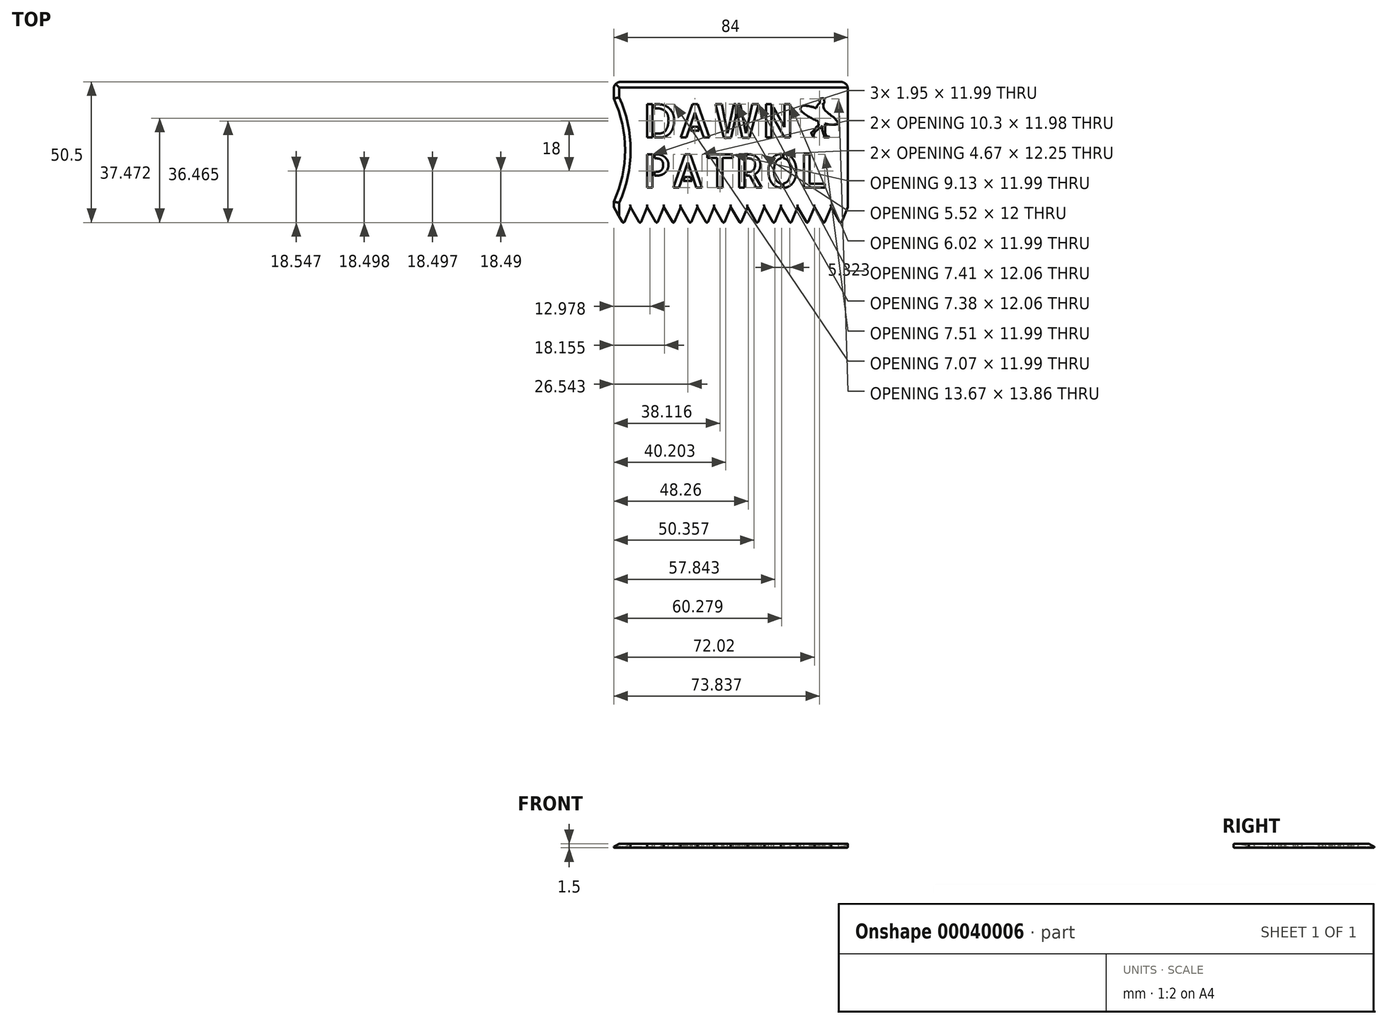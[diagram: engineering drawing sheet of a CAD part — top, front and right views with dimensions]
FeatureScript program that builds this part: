
annotation { "Feature Type Name" : "Feature", "Feature Type Description" : "" }
export const myFeature = defineFeature(function(context is Context, id is Id, definition is map)
    precondition{}
    {
        {
            assignVariable(context, id + "F0", {"name" : "t", "anyValue" : 1.5});
        }
        {
            var Q0;
            Q0=qCreatedBy(makeId("Top.planeOp"),FACE);
            var sketch = newSketch(context, id + "F1", { "sketchPlane" : qUnion([Q0])});
            skLineSegment(sketch, "E0.bottom", {"start": v(84, 51) * mm, "end": v(0, 51) * mm});
            skLineSegment(sketch, "E0.top", {"start": v(81.5, 0) * mm, "end": v(3.5, 0) * mm, "construction": true});
            skLineSegment(sketch, "E0.left", {"start": v(84, 51) * mm, "end": v(84, 6) * mm});
            skLineSegment(sketch, "E0.right", {"start": v(0, 51) * mm, "end": v(0, 6) * mm, "construction": true});
            skLineSegment(sketch, "E1", {"start": v(84, 6) * mm, "end": v(0, 6) * mm, "construction": true});
            skLineSegment(sketch, "E2", {"start": v(84, 6) * mm, "end": v(81.5, 0) * mm});
            skLineSegment(sketch, "E3", {"start": v(81.5, 0) * mm, "end": v(78, 6) * mm});
            skLineSegment(sketch, "E4.1.0.0", {"start": v(78, 6) * mm, "end": v(75.5, 0) * mm});
            skLineSegment(sketch, "E4.1.0.1", {"start": v(75.5, 0) * mm, "end": v(72, 6) * mm});
            skLineSegment(sketch, "E4.2.0.0", {"start": v(72, 6) * mm, "end": v(69.5, 0) * mm});
            skLineSegment(sketch, "E4.2.0.1", {"start": v(69.5, 0) * mm, "end": v(66, 6) * mm});
            skLineSegment(sketch, "E4.3.0.0", {"start": v(66, 6) * mm, "end": v(63.5, 0) * mm});
            skLineSegment(sketch, "E4.3.0.1", {"start": v(63.5, 0) * mm, "end": v(60, 6) * mm});
            skLineSegment(sketch, "E4.4.0.0", {"start": v(60, 6) * mm, "end": v(57.5, 0) * mm});
            skLineSegment(sketch, "E4.4.0.1", {"start": v(57.5, 0) * mm, "end": v(54, 6) * mm});
            skLineSegment(sketch, "E4.5.0.0", {"start": v(54, 6) * mm, "end": v(51.5, 0) * mm});
            skLineSegment(sketch, "E4.5.0.1", {"start": v(51.5, 0) * mm, "end": v(48, 6) * mm});
            skLineSegment(sketch, "E4.6.0.0", {"start": v(48, 6) * mm, "end": v(45.5, 0) * mm});
            skLineSegment(sketch, "E4.6.0.1", {"start": v(45.5, 0) * mm, "end": v(42, 6) * mm});
            skLineSegment(sketch, "E4.7.0.0", {"start": v(42, 6) * mm, "end": v(39.5, 0) * mm});
            skLineSegment(sketch, "E4.7.0.1", {"start": v(39.5, 0) * mm, "end": v(36, 6) * mm});
            skLineSegment(sketch, "E4.8.0.0", {"start": v(36, 6) * mm, "end": v(33.5, 0) * mm});
            skLineSegment(sketch, "E4.8.0.1", {"start": v(33.5, 0) * mm, "end": v(30, 6) * mm});
            skLineSegment(sketch, "E4.9.0.0", {"start": v(30, 6) * mm, "end": v(27.5, 0) * mm});
            skLineSegment(sketch, "E4.9.0.1", {"start": v(27.5, 0) * mm, "end": v(24, 6) * mm});
            skLineSegment(sketch, "E4.10.0.0", {"start": v(24, 6) * mm, "end": v(21.5, 0) * mm});
            skLineSegment(sketch, "E4.10.0.1", {"start": v(21.5, 0) * mm, "end": v(18, 6) * mm});
            skLineSegment(sketch, "E4.11.0.0", {"start": v(18, 6) * mm, "end": v(15.5, 0) * mm});
            skLineSegment(sketch, "E4.11.0.1", {"start": v(15.5, 0) * mm, "end": v(12, 6) * mm});
            skLineSegment(sketch, "E4.12.0.0", {"start": v(12, 6) * mm, "end": v(9.5, 0) * mm});
            skLineSegment(sketch, "E4.12.0.1", {"start": v(9.5, 0) * mm, "end": v(6, 6) * mm});
            skLineSegment(sketch, "E4.13.0.0", {"start": v(6, 6) * mm, "end": v(3.5, 0) * mm});
            skLineSegment(sketch, "E4.13.0.1", {"start": v(3.5, 0) * mm, "end": v(0, 6) * mm});
            skLineSegment(sketch, "E4.direction1", {"start": v(84, 6) * mm, "end": v(78, 6) * mm, "construction": true});
            skLineSegment(sketch, "E5", {"start": v(0, 6) * mm, "end": v(0, 8) * mm});
            skArc(sketch, "E6", {"start": v(0, 8) * mm, "mid": v(4.07, 26.5) * mm, "end": v(0, 45) * mm});
            skLineSegment(sketch, "E7", {"start": v(0, 45) * mm, "end": v(0, 51) * mm});
            skLineSegment(sketch, "E8", {"start": v(0, 6) * mm, "end": v(0, 0) * mm, "construction": true});
            skSolve(sketch);
        }
        {
            var Q0;
            Q0=qSketchRegion(id+"F1",true);
            extrude(context, id + "F2", {"entities" : qUnion([Q0]), "depth" : (getVariable(context, 't')) * mm});
        }
        {
            var Q0;
            Q0=makeQuery(id+"F2.opExtrude","CAP_EDGE",EDGE,{"disambiguationData":[OSD([sQuery(id+"F1.wireOp",EDGE,"E5")])],"isStart":false});
            var Q1;
            Q1=makeQuery(id+"F2.opExtrude","CAP_EDGE",EDGE,{"disambiguationData":[OSD([sQuery(id+"F1.wireOp",EDGE,"E6")])],"isStart":false});
            var Q2;
            Q2=makeQuery(id+"F2.opExtrude","CAP_EDGE",EDGE,{"disambiguationData":[OSD([sQuery(id+"F1.wireOp",EDGE,"E0.bottom")])],"isStart":false});
            var Q3;
            Q3=makeQuery(id+"F2.opExtrude","CAP_EDGE",EDGE,{"disambiguationData":[OSD([sQuery(id+"F1.wireOp",EDGE,"E7")])],"isStart":false});
            chamfer(context, id + "F3", {"entities" : qUnion([Q0, Q1, Q2, Q3]), "chamferType" : ChamferType.TWO_OFFSETS, "width1" : (getVariable(context, 't') * 2.2 / 3) * mm, "oppositeDirection" : false, "width2" : (getVariable(context, 't') * 4 / 3) * mm, "tangentPropagation" : true});
        }
        {
            var Q0;
            Q0=makeQuery(id+"F2.opExtrude","SWEPT_EDGE",EDGE,{"disambiguationData":[OSD([sQuery(id+"F1.wireOp",EDGE,"E0.bottom"),sQuery(id+"F1.wireOp",EDGE,"E7")])]});
            var Q1;
            Q1=makeQuery(id+"F2.opExtrude","SWEPT_EDGE",EDGE,{"disambiguationData":[OSD([sQuery(id+"F1.wireOp",EDGE,"E0.bottom"),sQuery(id+"F1.wireOp",EDGE,"E0.left")])]});
            fillet(context, id + "F4", {"entities" : qUnion([Q0, Q1]), "radius" : 2.5 * mm, "tangentPropagation" : true, "allowEdgeOverflow" : false});
        }
        {
            var Q0;
            Q0=makeQuery(id+"F2.opExtrude","CAP_FACE",FACE,{"disambiguationData":[OSD([sQuery(id+"F1.wireOp",EDGE,"E0.bottom"),sQuery(id+"F1.wireOp",EDGE,"E0.left"),sQuery(id+"F1.wireOp",EDGE,"E2"),sQuery(id+"F1.wireOp",EDGE,"E3"),sQuery(id+"F1.wireOp",EDGE,"E4.1.0.0"),sQuery(id+"F1.wireOp",EDGE,"E4.1.0.1"),sQuery(id+"F1.wireOp",EDGE,"E4.2.0.0"),sQuery(id+"F1.wireOp",EDGE,"E4.2.0.1"),sQuery(id+"F1.wireOp",EDGE,"E4.3.0.0"),sQuery(id+"F1.wireOp",EDGE,"E4.3.0.1"),sQuery(id+"F1.wireOp",EDGE,"E4.4.0.0"),sQuery(id+"F1.wireOp",EDGE,"E4.4.0.1"),sQuery(id+"F1.wireOp",EDGE,"E4.5.0.0"),sQuery(id+"F1.wireOp",EDGE,"E4.5.0.1"),sQuery(id+"F1.wireOp",EDGE,"E4.6.0.0"),sQuery(id+"F1.wireOp",EDGE,"E4.6.0.1"),sQuery(id+"F1.wireOp",EDGE,"E4.7.0.0"),sQuery(id+"F1.wireOp",EDGE,"E4.7.0.1"),sQuery(id+"F1.wireOp",EDGE,"E4.8.0.0"),sQuery(id+"F1.wireOp",EDGE,"E4.8.0.1"),sQuery(id+"F1.wireOp",EDGE,"E4.9.0.0"),sQuery(id+"F1.wireOp",EDGE,"E4.9.0.1"),sQuery(id+"F1.wireOp",EDGE,"E4.10.0.0"),sQuery(id+"F1.wireOp",EDGE,"E4.10.0.1"),sQuery(id+"F1.wireOp",EDGE,"E4.11.0.0"),sQuery(id+"F1.wireOp",EDGE,"E4.11.0.1"),sQuery(id+"F1.wireOp",EDGE,"E4.12.0.0"),sQuery(id+"F1.wireOp",EDGE,"E4.12.0.1"),sQuery(id+"F1.wireOp",EDGE,"E4.13.0.0"),sQuery(id+"F1.wireOp",EDGE,"E4.13.0.1"),sQuery(id+"F1.wireOp",EDGE,"E5"),sQuery(id+"F1.wireOp",EDGE,"E6"),sQuery(id+"F1.wireOp",EDGE,"E7")])],"isStart":false});
            var sketch = newSketch(context, id + "F5", { "sketchPlane" : qUnion([Q0])});
            skLineSegment(sketch, "E9.0", {"start": v(81.9, 6.42) * mm, "end": v(81.9, 46.9) * mm});
            skLineSegment(sketch, "E9.1", {"start": v(81.19, 4.7) * mm, "end": v(81.9, 6.42) * mm});
            skLineSegment(sketch, "E9.2", {"start": v(77.69, 10.7) * mm, "end": v(81.19, 4.7) * mm});
            skLineSegment(sketch, "E9.3", {"start": v(75.19, 4.7) * mm, "end": v(77.69, 10.7) * mm});
            skLineSegment(sketch, "E9.4", {"start": v(71.69, 10.7) * mm, "end": v(75.19, 4.7) * mm});
            skLineSegment(sketch, "E9.5", {"start": v(69.19, 4.7) * mm, "end": v(71.69, 10.7) * mm});
            skLineSegment(sketch, "E9.6", {"start": v(65.69, 10.7) * mm, "end": v(69.19, 4.7) * mm});
            skLineSegment(sketch, "E9.7", {"start": v(81.9, 46.9) * mm, "end": v(3.64, 46.9) * mm});
            skArc(sketch, "E9.8", {"start": v(3.64, 46.9) * mm, "mid": v(8.1, 29.09) * mm, "end": v(5.57, 10.9) * mm});
            skLineSegment(sketch, "E9.9", {"start": v(5.57, 10.9) * mm, "end": v(9.19, 4.7) * mm});
            skLineSegment(sketch, "E9.10", {"start": v(9.19, 4.7) * mm, "end": v(11.69, 10.7) * mm});
            skLineSegment(sketch, "E9.11", {"start": v(11.69, 10.7) * mm, "end": v(15.19, 4.7) * mm});
            skLineSegment(sketch, "E9.12", {"start": v(15.19, 4.7) * mm, "end": v(17.69, 10.7) * mm});
            skLineSegment(sketch, "E9.13", {"start": v(17.69, 10.7) * mm, "end": v(21.19, 4.7) * mm});
            skLineSegment(sketch, "E9.14", {"start": v(21.19, 4.7) * mm, "end": v(23.69, 10.7) * mm});
            skLineSegment(sketch, "E9.15", {"start": v(23.69, 10.7) * mm, "end": v(27.19, 4.7) * mm});
            skLineSegment(sketch, "E9.16", {"start": v(27.19, 4.7) * mm, "end": v(29.69, 10.7) * mm});
            skLineSegment(sketch, "E9.17", {"start": v(29.69, 10.7) * mm, "end": v(33.19, 4.7) * mm});
            skLineSegment(sketch, "E9.18", {"start": v(33.19, 4.7) * mm, "end": v(35.69, 10.7) * mm});
            skLineSegment(sketch, "E9.19", {"start": v(35.69, 10.7) * mm, "end": v(39.19, 4.7) * mm});
            skLineSegment(sketch, "E9.20", {"start": v(39.19, 4.7) * mm, "end": v(41.69, 10.7) * mm});
            skLineSegment(sketch, "E9.21", {"start": v(41.69, 10.7) * mm, "end": v(45.19, 4.7) * mm});
            skLineSegment(sketch, "E9.22", {"start": v(45.19, 4.7) * mm, "end": v(47.69, 10.7) * mm});
            skLineSegment(sketch, "E9.23", {"start": v(47.69, 10.7) * mm, "end": v(51.19, 4.7) * mm});
            skLineSegment(sketch, "E9.24", {"start": v(51.19, 4.7) * mm, "end": v(53.69, 10.7) * mm});
            skLineSegment(sketch, "E9.25", {"start": v(53.69, 10.7) * mm, "end": v(57.19, 4.7) * mm});
            skLineSegment(sketch, "E9.26", {"start": v(57.19, 4.7) * mm, "end": v(59.69, 10.7) * mm});
            skLineSegment(sketch, "E9.27", {"start": v(59.69, 10.7) * mm, "end": v(63.19, 4.7) * mm});
            skLineSegment(sketch, "E9.28", {"start": v(63.19, 4.7) * mm, "end": v(65.69, 10.7) * mm});
            skSolve(sketch);
        }
        {
            var Q0;
            Q0=makeQuery(id+"F2.opExtrude","CAP_FACE",FACE,{"disambiguationData":[OSD([sQuery(id+"F1.wireOp",EDGE,"E0.bottom"),sQuery(id+"F1.wireOp",EDGE,"E0.left"),sQuery(id+"F1.wireOp",EDGE,"E2"),sQuery(id+"F1.wireOp",EDGE,"E3"),sQuery(id+"F1.wireOp",EDGE,"E4.1.0.0"),sQuery(id+"F1.wireOp",EDGE,"E4.1.0.1"),sQuery(id+"F1.wireOp",EDGE,"E4.2.0.0"),sQuery(id+"F1.wireOp",EDGE,"E4.2.0.1"),sQuery(id+"F1.wireOp",EDGE,"E4.3.0.0"),sQuery(id+"F1.wireOp",EDGE,"E4.3.0.1"),sQuery(id+"F1.wireOp",EDGE,"E4.4.0.0"),sQuery(id+"F1.wireOp",EDGE,"E4.4.0.1"),sQuery(id+"F1.wireOp",EDGE,"E4.5.0.0"),sQuery(id+"F1.wireOp",EDGE,"E4.5.0.1"),sQuery(id+"F1.wireOp",EDGE,"E4.6.0.0"),sQuery(id+"F1.wireOp",EDGE,"E4.6.0.1"),sQuery(id+"F1.wireOp",EDGE,"E4.7.0.0"),sQuery(id+"F1.wireOp",EDGE,"E4.7.0.1"),sQuery(id+"F1.wireOp",EDGE,"E4.8.0.0"),sQuery(id+"F1.wireOp",EDGE,"E4.8.0.1"),sQuery(id+"F1.wireOp",EDGE,"E4.9.0.0"),sQuery(id+"F1.wireOp",EDGE,"E4.9.0.1"),sQuery(id+"F1.wireOp",EDGE,"E4.10.0.0"),sQuery(id+"F1.wireOp",EDGE,"E4.10.0.1"),sQuery(id+"F1.wireOp",EDGE,"E4.11.0.0"),sQuery(id+"F1.wireOp",EDGE,"E4.11.0.1"),sQuery(id+"F1.wireOp",EDGE,"E4.12.0.0"),sQuery(id+"F1.wireOp",EDGE,"E4.12.0.1"),sQuery(id+"F1.wireOp",EDGE,"E4.13.0.0"),sQuery(id+"F1.wireOp",EDGE,"E4.13.0.1"),sQuery(id+"F1.wireOp",EDGE,"E5"),sQuery(id+"F1.wireOp",EDGE,"E6"),sQuery(id+"F1.wireOp",EDGE,"E7")])],"isStart":true});
            var Q1;
            Q1=makeQuery(id+"F2.opExtrude","CAP_EDGE",EDGE,{"disambiguationData":[OSD([sQuery(id+"F1.wireOp",EDGE,"E4.13.0.1")])],"isStart":false});
            var Q2;
            Q2=makeQuery(id+"F2.opExtrude","CAP_EDGE",EDGE,{"disambiguationData":[OSD([sQuery(id+"F1.wireOp",EDGE,"E4.13.0.0")])],"isStart":false});
            var Q3;
            Q3=makeQuery(id+"F2.opExtrude","SWEPT_EDGE",EDGE,{"disambiguationData":[OSD([sQuery(id+"F1.wireOp",EDGE,"E4.13.0.0"),sQuery(id+"F1.wireOp",EDGE,"E4.13.0.1")])]});
            var Q4;
            Q4=makeQuery(id+"F2.opExtrude","CAP_EDGE",EDGE,{"disambiguationData":[OSD([sQuery(id+"F1.wireOp",EDGE,"E4.12.0.1")])],"isStart":false});
            var Q5;
            Q5=makeQuery(id+"F2.opExtrude","SWEPT_EDGE",EDGE,{"disambiguationData":[OSD([sQuery(id+"F1.wireOp",EDGE,"E4.12.0.0"),sQuery(id+"F1.wireOp",EDGE,"E4.12.0.1")])]});
            var Q6;
            Q6=makeQuery(id+"F2.opExtrude","CAP_EDGE",EDGE,{"disambiguationData":[OSD([sQuery(id+"F1.wireOp",EDGE,"E4.12.0.0")])],"isStart":false});
            var Q7;
            Q7=makeQuery(id+"F2.opExtrude","CAP_EDGE",EDGE,{"disambiguationData":[OSD([sQuery(id+"F1.wireOp",EDGE,"E4.11.0.1")])],"isStart":false});
            var Q8;
            Q8=makeQuery(id+"F2.opExtrude","SWEPT_EDGE",EDGE,{"disambiguationData":[OSD([sQuery(id+"F1.wireOp",EDGE,"E4.11.0.0"),sQuery(id+"F1.wireOp",EDGE,"E4.11.0.1")])]});
            var Q9;
            Q9=makeQuery(id+"F2.opExtrude","CAP_EDGE",EDGE,{"disambiguationData":[OSD([sQuery(id+"F1.wireOp",EDGE,"E4.11.0.0")])],"isStart":false});
            var Q10;
            Q10=makeQuery(id+"F2.opExtrude","CAP_EDGE",EDGE,{"disambiguationData":[OSD([sQuery(id+"F1.wireOp",EDGE,"E4.10.0.1")])],"isStart":false});
            var Q11;
            Q11=makeQuery(id+"F2.opExtrude","CAP_EDGE",EDGE,{"disambiguationData":[OSD([sQuery(id+"F1.wireOp",EDGE,"E4.10.0.0")])],"isStart":false});
            var Q12;
            Q12=makeQuery(id+"F2.opExtrude","CAP_EDGE",EDGE,{"disambiguationData":[OSD([sQuery(id+"F1.wireOp",EDGE,"E4.9.0.1")])],"isStart":false});
            var Q13;
            Q13=makeQuery(id+"F2.opExtrude","CAP_EDGE",EDGE,{"disambiguationData":[OSD([sQuery(id+"F1.wireOp",EDGE,"E4.9.0.0")])],"isStart":false});
            var Q14;
            Q14=makeQuery(id+"F2.opExtrude","CAP_EDGE",EDGE,{"disambiguationData":[OSD([sQuery(id+"F1.wireOp",EDGE,"E4.8.0.1")])],"isStart":false});
            var Q15;
            Q15=makeQuery(id+"F2.opExtrude","CAP_EDGE",EDGE,{"disambiguationData":[OSD([sQuery(id+"F1.wireOp",EDGE,"E4.8.0.0")])],"isStart":false});
            var Q16;
            Q16=makeQuery(id+"F2.opExtrude","CAP_EDGE",EDGE,{"disambiguationData":[OSD([sQuery(id+"F1.wireOp",EDGE,"E4.7.0.1")])],"isStart":false});
            var Q17;
            Q17=makeQuery(id+"F2.opExtrude","CAP_EDGE",EDGE,{"disambiguationData":[OSD([sQuery(id+"F1.wireOp",EDGE,"E4.7.0.0")])],"isStart":false});
            var Q18;
            Q18=makeQuery(id+"F2.opExtrude","CAP_EDGE",EDGE,{"disambiguationData":[OSD([sQuery(id+"F1.wireOp",EDGE,"E4.6.0.1")])],"isStart":false});
            var Q19;
            Q19=makeQuery(id+"F2.opExtrude","CAP_EDGE",EDGE,{"disambiguationData":[OSD([sQuery(id+"F1.wireOp",EDGE,"E4.6.0.0")])],"isStart":false});
            var Q20;
            Q20=makeQuery(id+"F2.opExtrude","CAP_EDGE",EDGE,{"disambiguationData":[OSD([sQuery(id+"F1.wireOp",EDGE,"E4.5.0.1")])],"isStart":false});
            var Q21;
            Q21=makeQuery(id+"F2.opExtrude","CAP_EDGE",EDGE,{"disambiguationData":[OSD([sQuery(id+"F1.wireOp",EDGE,"E4.5.0.0")])],"isStart":false});
            var Q22;
            Q22=makeQuery(id+"F2.opExtrude","CAP_EDGE",EDGE,{"disambiguationData":[OSD([sQuery(id+"F1.wireOp",EDGE,"E4.4.0.1")])],"isStart":false});
            var Q23;
            Q23=makeQuery(id+"F2.opExtrude","CAP_EDGE",EDGE,{"disambiguationData":[OSD([sQuery(id+"F1.wireOp",EDGE,"E4.4.0.0")])],"isStart":false});
            var Q24;
            Q24=makeQuery(id+"F2.opExtrude","CAP_EDGE",EDGE,{"disambiguationData":[OSD([sQuery(id+"F1.wireOp",EDGE,"E4.3.0.1")])],"isStart":false});
            var Q25;
            Q25=makeQuery(id+"F2.opExtrude","CAP_EDGE",EDGE,{"disambiguationData":[OSD([sQuery(id+"F1.wireOp",EDGE,"E4.3.0.0")])],"isStart":false});
            var Q26;
            Q26=makeQuery(id+"F2.opExtrude","CAP_EDGE",EDGE,{"disambiguationData":[OSD([sQuery(id+"F1.wireOp",EDGE,"E4.2.0.1")])],"isStart":false});
            var Q27;
            Q27=makeQuery(id+"F2.opExtrude","CAP_EDGE",EDGE,{"disambiguationData":[OSD([sQuery(id+"F1.wireOp",EDGE,"E4.2.0.0")])],"isStart":false});
            var Q28;
            Q28=makeQuery(id+"F2.opExtrude","CAP_EDGE",EDGE,{"disambiguationData":[OSD([sQuery(id+"F1.wireOp",EDGE,"E4.1.0.1")])],"isStart":false});
            var Q29;
            Q29=makeQuery(id+"F2.opExtrude","CAP_EDGE",EDGE,{"disambiguationData":[OSD([sQuery(id+"F1.wireOp",EDGE,"E4.1.0.0")])],"isStart":false});
            var Q30;
            Q30=makeQuery(id+"F2.opExtrude","CAP_EDGE",EDGE,{"disambiguationData":[OSD([sQuery(id+"F1.wireOp",EDGE,"E3")])],"isStart":false});
            var Q31;
            Q31=makeQuery(id+"F2.opExtrude","SWEPT_EDGE",EDGE,{"disambiguationData":[OSD([sQuery(id+"F1.wireOp",EDGE,"E2"),sQuery(id+"F1.wireOp",EDGE,"E3")])]});
            var Q32;
            Q32=makeQuery(id+"F2.opExtrude","CAP_EDGE",EDGE,{"disambiguationData":[OSD([sQuery(id+"F1.wireOp",EDGE,"E2")])],"isStart":false});
            var Q33;
            Q33=makeQuery(id+"F2.opExtrude","SWEPT_EDGE",EDGE,{"disambiguationData":[OSD([sQuery(id+"F1.wireOp",EDGE,"E4.1.0.0"),sQuery(id+"F1.wireOp",EDGE,"E4.1.0.1")])]});
            var Q34;
            Q34=makeQuery(id+"F2.opExtrude","SWEPT_EDGE",EDGE,{"disambiguationData":[OSD([sQuery(id+"F1.wireOp",EDGE,"E4.2.0.0"),sQuery(id+"F1.wireOp",EDGE,"E4.2.0.1")])]});
            var Q35;
            Q35=makeQuery(id+"F2.opExtrude","SWEPT_EDGE",EDGE,{"disambiguationData":[OSD([sQuery(id+"F1.wireOp",EDGE,"E4.3.0.0"),sQuery(id+"F1.wireOp",EDGE,"E4.3.0.1")])]});
            var Q36;
            Q36=makeQuery(id+"F2.opExtrude","SWEPT_EDGE",EDGE,{"disambiguationData":[OSD([sQuery(id+"F1.wireOp",EDGE,"E4.4.0.0"),sQuery(id+"F1.wireOp",EDGE,"E4.4.0.1")])]});
            var Q37;
            Q37=makeQuery(id+"F2.opExtrude","SWEPT_EDGE",EDGE,{"disambiguationData":[OSD([sQuery(id+"F1.wireOp",EDGE,"E4.5.0.0"),sQuery(id+"F1.wireOp",EDGE,"E4.5.0.1")])]});
            var Q38;
            Q38=makeQuery(id+"F2.opExtrude","SWEPT_EDGE",EDGE,{"disambiguationData":[OSD([sQuery(id+"F1.wireOp",EDGE,"E4.6.0.0"),sQuery(id+"F1.wireOp",EDGE,"E4.6.0.1")])]});
            var Q39;
            Q39=makeQuery(id+"F2.opExtrude","SWEPT_EDGE",EDGE,{"disambiguationData":[OSD([sQuery(id+"F1.wireOp",EDGE,"E4.7.0.0"),sQuery(id+"F1.wireOp",EDGE,"E4.7.0.1")])]});
            var Q40;
            Q40=makeQuery(id+"F2.opExtrude","SWEPT_EDGE",EDGE,{"disambiguationData":[OSD([sQuery(id+"F1.wireOp",EDGE,"E4.8.0.0"),sQuery(id+"F1.wireOp",EDGE,"E4.8.0.1")])]});
            var Q41;
            Q41=makeQuery(id+"F2.opExtrude","SWEPT_EDGE",EDGE,{"disambiguationData":[OSD([sQuery(id+"F1.wireOp",EDGE,"E4.9.0.0"),sQuery(id+"F1.wireOp",EDGE,"E4.9.0.1")])]});
            var Q42;
            Q42=makeQuery(id+"F2.opExtrude","SWEPT_EDGE",EDGE,{"disambiguationData":[OSD([sQuery(id+"F1.wireOp",EDGE,"E4.10.0.0"),sQuery(id+"F1.wireOp",EDGE,"E4.10.0.1")])]});
            fillet(context, id + "F6", {"entities" : qUnion([Q0, Q1, Q2, Q3, Q4, Q5, Q6, Q7, Q8, Q9, Q10, Q11, Q12, Q13, Q14, Q15, Q16, Q17, Q18, Q19, Q20, Q21, Q22, Q23, Q24, Q25, Q26, Q27, Q28, Q29, Q30, Q31, Q32, Q33, Q34, Q35, Q36, Q37, Q38, Q39, Q40, Q41, Q42]), "radius" : .4 * mm, "tangentPropagation" : true, "allowEdgeOverflow" : false});
        }
        {
            var Q0;
            Q0=makeQuery(id+"F2.opExtrude","CAP_FACE",FACE,{"disambiguationData":[OSD([sQuery(id+"F1.wireOp",EDGE,"E0.bottom"),sQuery(id+"F1.wireOp",EDGE,"E0.left"),sQuery(id+"F1.wireOp",EDGE,"E2"),sQuery(id+"F1.wireOp",EDGE,"E3"),sQuery(id+"F1.wireOp",EDGE,"E4.1.0.0"),sQuery(id+"F1.wireOp",EDGE,"E4.1.0.1"),sQuery(id+"F1.wireOp",EDGE,"E4.2.0.0"),sQuery(id+"F1.wireOp",EDGE,"E4.2.0.1"),sQuery(id+"F1.wireOp",EDGE,"E4.3.0.0"),sQuery(id+"F1.wireOp",EDGE,"E4.3.0.1"),sQuery(id+"F1.wireOp",EDGE,"E4.4.0.0"),sQuery(id+"F1.wireOp",EDGE,"E4.4.0.1"),sQuery(id+"F1.wireOp",EDGE,"E4.5.0.0"),sQuery(id+"F1.wireOp",EDGE,"E4.5.0.1"),sQuery(id+"F1.wireOp",EDGE,"E4.6.0.0"),sQuery(id+"F1.wireOp",EDGE,"E4.6.0.1"),sQuery(id+"F1.wireOp",EDGE,"E4.7.0.0"),sQuery(id+"F1.wireOp",EDGE,"E4.7.0.1"),sQuery(id+"F1.wireOp",EDGE,"E4.8.0.0"),sQuery(id+"F1.wireOp",EDGE,"E4.8.0.1"),sQuery(id+"F1.wireOp",EDGE,"E4.9.0.0"),sQuery(id+"F1.wireOp",EDGE,"E4.9.0.1"),sQuery(id+"F1.wireOp",EDGE,"E4.10.0.0"),sQuery(id+"F1.wireOp",EDGE,"E4.10.0.1"),sQuery(id+"F1.wireOp",EDGE,"E4.11.0.0"),sQuery(id+"F1.wireOp",EDGE,"E4.11.0.1"),sQuery(id+"F1.wireOp",EDGE,"E4.12.0.0"),sQuery(id+"F1.wireOp",EDGE,"E4.12.0.1"),sQuery(id+"F1.wireOp",EDGE,"E4.13.0.0"),sQuery(id+"F1.wireOp",EDGE,"E4.13.0.1"),sQuery(id+"F1.wireOp",EDGE,"E5"),sQuery(id+"F1.wireOp",EDGE,"E6"),sQuery(id+"F1.wireOp",EDGE,"E7")])],"isStart":false});
            var sketch = newSketch(context, id + "F7", { "sketchPlane" : qUnion([Q0])});
            skText(sketch, "E10", { "text": "PATROL", "fontName": "AllertaStencil-Regular.ttf"});
            skText(sketch, "E11", { "text": "DAWN", "fontName": "AllertaStencil-Regular.ttf"});
            const initialGuessF7  = {"E10": [0.01052, 0.013, 1, 0, 0.012], "E11": [0.01044, 0.031, 1, 0, 0.012]};
            skSetInitialGuess(sketch, initialGuessF7);
            skSolve(sketch);
        }
        {
            var Q0;
            Q0 = qSketchRegion(id + "F7", true);
            extrude(context, id + "F8", {"entities" : qUnion([Q0]), "operationType" : NewBodyOperationType.REMOVE, "endBound" : BoundingType.THROUGH_ALL, "oppositeDirection" : true, "depth" : 25 * mm});
        }
        {
            var Q0;
            Q0=makeQuery(id+"F2.opExtrude","CAP_FACE",FACE,{"disambiguationData":[OSD([sQuery(id+"F1.wireOp",EDGE,"E0.bottom"),sQuery(id+"F1.wireOp",EDGE,"E0.left"),sQuery(id+"F1.wireOp",EDGE,"E2"),sQuery(id+"F1.wireOp",EDGE,"E3"),sQuery(id+"F1.wireOp",EDGE,"E4.1.0.0"),sQuery(id+"F1.wireOp",EDGE,"E4.1.0.1"),sQuery(id+"F1.wireOp",EDGE,"E4.2.0.0"),sQuery(id+"F1.wireOp",EDGE,"E4.2.0.1"),sQuery(id+"F1.wireOp",EDGE,"E4.3.0.0"),sQuery(id+"F1.wireOp",EDGE,"E4.3.0.1"),sQuery(id+"F1.wireOp",EDGE,"E4.4.0.0"),sQuery(id+"F1.wireOp",EDGE,"E4.4.0.1"),sQuery(id+"F1.wireOp",EDGE,"E4.5.0.0"),sQuery(id+"F1.wireOp",EDGE,"E4.5.0.1"),sQuery(id+"F1.wireOp",EDGE,"E4.6.0.0"),sQuery(id+"F1.wireOp",EDGE,"E4.6.0.1"),sQuery(id+"F1.wireOp",EDGE,"E4.7.0.0"),sQuery(id+"F1.wireOp",EDGE,"E4.7.0.1"),sQuery(id+"F1.wireOp",EDGE,"E4.8.0.0"),sQuery(id+"F1.wireOp",EDGE,"E4.8.0.1"),sQuery(id+"F1.wireOp",EDGE,"E4.9.0.0"),sQuery(id+"F1.wireOp",EDGE,"E4.9.0.1"),sQuery(id+"F1.wireOp",EDGE,"E4.10.0.0"),sQuery(id+"F1.wireOp",EDGE,"E4.10.0.1"),sQuery(id+"F1.wireOp",EDGE,"E4.11.0.0"),sQuery(id+"F1.wireOp",EDGE,"E4.11.0.1"),sQuery(id+"F1.wireOp",EDGE,"E4.12.0.0"),sQuery(id+"F1.wireOp",EDGE,"E4.12.0.1"),sQuery(id+"F1.wireOp",EDGE,"E4.13.0.0"),sQuery(id+"F1.wireOp",EDGE,"E4.13.0.1"),sQuery(id+"F1.wireOp",EDGE,"E5"),sQuery(id+"F1.wireOp",EDGE,"E6"),sQuery(id+"F1.wireOp",EDGE,"E7")])],"isStart":false});
            var sketch = newSketch(context, id + "F9", { "sketchPlane" : qUnion([Q0])});
            skLineSegment(sketch, "E12", {"start": v(66.95, 41.84) * mm, "end": v(80.97, 35.81) * mm, "construction": true});
            skFitSpline(sketch, "E13", {"points": [v(73.4, 36.87) * mm, v(70.8, 38.04) * mm, v(68.82, 39.24) * mm, v(67.19, 40.67) * mm, v(67, 41.22) * mm, v(67.13, 41.76) * mm], "startDerivative": vector(-8.18, 3.62) * mm, "endDerivative": vector(1.44, 4.42) * mm});
            skFitSpline(sketch, "E14", {"points": [v(74.41, 40.85) * mm, v(72.35, 41.67) * mm, v(70.12, 42.27) * mm, v(67.96, 42.47) * mm, v(67.44, 42.23) * mm, v(67.13, 41.76) * mm], "startDerivative": vector(-8.26, 3.44) * mm, "endDerivative": vector(-2.21, -4.08) * mm});
            skFitSpline(sketch, "E15", {"points": [v(73.4, 36.87) * mm, v(73.4, 36.1) * mm, v(73.57, 35.54) * mm, v(73.58, 35.27) * mm, v(73.43, 35.13) * mm, v(72.87, 34.87) * mm, v(72.4, 34.35) * mm, v(71.97, 33.73) * mm, v(71.61, 33.29) * mm, v(71.4, 33.12) * mm, v(71.1, 33) * mm, v(70.89, 32.9) * mm, v(70.83, 32.74) * mm, v(70.94, 32.4) * mm, v(71.1, 32.24) * mm, v(71.23, 32.12) * mm, v(71.27, 31.92) * mm, v(71.3, 31.52) * mm, v(71.46, 31.31) * mm, v(71.67, 31.2) * mm, v(71.95, 31.15) * mm, v(72, 31.18) * mm, v(72, 31.22) * mm, v(71.98, 31.3) * mm, v(71.86, 31.39) * mm, v(71.75, 31.5) * mm, v(71.73, 31.78) * mm, v(71.76, 32.1) * mm, v(71.8, 32.32) * mm, v(71.87, 32.48) * mm, v(72.07, 32.78) * mm, v(72.6, 33.3) * mm, v(73.2, 33.79) * mm, v(73.8, 34.23) * mm, v(74.35, 34.55) * mm, v(74.58, 34.75) * mm, v(74.67, 34.97) * mm, v(74.71, 35.17) * mm, v(74.77, 35.2) * mm, v(74.8, 35.2) * mm], "startDerivative": vector(-1.7, -19.21) * mm, "endDerivative": vector(3.01, -1.59) * mm});
            skFitSpline(sketch, "E16", {"points": [v(72.67, 41.55) * mm, v(72.93, 42.2) * mm, v(73.19, 42.72) * mm, v(73.47, 43.01) * mm, v(73.77, 43.26) * mm, v(73.98, 43.44) * mm, v(74.04, 43.56) * mm, v(73.93, 43.82) * mm, v(73.83, 44.16) * mm, v(73.88, 44.56) * mm, v(74.04, 44.88) * mm, v(74.58, 45.2) * mm, v(75.03, 45.12) * mm, v(75.35, 44.99) * mm, v(75.57, 44.76) * mm, v(75.55, 44.54) * mm, v(75.49, 44.42) * mm, v(75.55, 44.3) * mm, v(75.58, 44.15) * mm, v(75.53, 44.07) * mm, v(75.52, 44) * mm, v(75.6, 43.9) * mm, v(75.68, 43.78) * mm, v(75.68, 43.7) * mm, v(75.64, 43.64) * mm, v(75.52, 43.66) * mm, v(75.5, 43.6) * mm, v(75.5, 43.5) * mm, v(75.48, 43.43) * mm, v(75.43, 43.37) * mm, v(75.44, 43.28) * mm, v(75.47, 43.19) * mm, v(75.45, 43.12) * mm, v(75.36, 43.09) * mm, v(75.27, 43.05) * mm, v(75.09, 43.06) * mm, v(75, 43.08) * mm, v(74.93, 43.03) * mm, v(74.99, 42.93) * mm, v(75.15, 42.77) * mm, v(75.29, 42.44) * mm, v(75.3, 41.91) * mm, v(75.41, 41.43) * mm, v(75.64, 40.98) * mm, v(76.11, 40.51) * mm, v(76.5, 40.15) * mm, v(76.93, 39.85) * mm, v(77.24, 39.52) * mm, v(77.5, 39.4) * mm, v(77.82, 39.27) * mm, v(77.93, 39.07) * mm, v(77.96, 38.96) * mm], "startDerivative": vector(7.84, 19.36) * mm, "endDerivative": vector(2.4, -8.81) * mm});
            skFitSpline(sketch, "E17", {"points": [v(75.73, 36.07) * mm, v(76.39, 35.89) * mm, v(77.35, 35.68) * mm, v(78.3, 35.58) * mm, v(79.13, 35.62) * mm, v(80.02, 35.74) * mm, v(80.65, 35.9) * mm, v(80.67, 35.94) * mm], "startDerivative": vector(4.26, -1.27) * mm, "endDerivative": vector(0.24, 0.98) * mm});
            skFitSpline(sketch, "E18.MirrorCS", {"points": [v(77.18, 39.44) * mm, v(77.77, 39.09) * mm, v(78.58, 38.53) * mm, v(79.3, 37.92) * mm, v(79.85, 37.29) * mm, v(80.37, 36.56) * mm, v(80.68, 35.99) * mm, v(80.67, 35.94) * mm], "startDerivative": vector(3.85, -2.22) * mm, "endDerivative": vector(-0.55, -0.85) * mm});
            skFitSpline(sketch, "E19", {"points": [v(75.73, 36.07) * mm, v(75.84, 35.6) * mm, v(75.9, 35.3) * mm, v(75.88, 34.86) * mm, v(75.84, 34.23) * mm, v(75.85, 33.54) * mm, v(75.9, 32.74) * mm, v(76.03, 32.08) * mm, v(76.2, 31.77) * mm, v(76.47, 31.57) * mm, v(76.72, 31.41) * mm, v(77.02, 31.34) * mm, v(77.25, 31.32) * mm, v(77.35, 31.3) * mm, v(77.35, 31.22) * mm, v(77.3, 31.14) * mm, v(77.19, 31.09) * mm, v(77.02, 31.05) * mm, v(76.72, 31.04) * mm, v(76.27, 31.04) * mm, v(75.96, 31.06) * mm, v(75.71, 31.05) * mm, v(75.55, 31.06) * mm, v(75.46, 31.1) * mm, v(75.41, 31.23) * mm, v(75.42, 31.4) * mm, v(75.49, 31.58) * mm, v(75.5, 31.76) * mm, v(75.37, 32.09) * mm, v(75.16, 32.66) * mm, v(74.97, 33.33) * mm, v(74.83, 33.98) * mm, v(74.88, 34.56) * mm, v(74.9, 34.97) * mm, v(74.88, 35.14) * mm, v(74.8, 35.2) * mm], "startDerivative": vector(2.94, -13.83) * mm, "endDerivative": vector(-5.6, 2.93) * mm});
            skSolve(sketch);
        }
        {
            var Q0;
            Q0=makeQuery(id+"F9.imprint","IMPRINT",FACE,{"disambiguationData":[TD([[makeQuery(id+"F9.imprint","IMPRINT",EDGE,{"derivedFrom":sQuery(id+"F9.wireOp",EDGE,"E13")}),-1.0]])]});
            var Q1;
            {var subQ0=sQuery(id+"F1.wireOp",EDGE,"E7");var subQ1=sQuery(id+"F1.wireOp",EDGE,"E6");var subQ2=sQuery(id+"F1.wireOp",EDGE,"E5");var subQ3=sQuery(id+"F1.wireOp",EDGE,"E4.13.0.1");var subQ4=sQuery(id+"F1.wireOp",EDGE,"E4.13.0.0");var subQ5=sQuery(id+"F1.wireOp",EDGE,"E4.12.0.1");var subQ6=sQuery(id+"F1.wireOp",EDGE,"E4.12.0.0");var subQ7=sQuery(id+"F1.wireOp",EDGE,"E4.11.0.1");var subQ8=sQuery(id+"F1.wireOp",EDGE,"E4.11.0.0");var subQ9=sQuery(id+"F1.wireOp",EDGE,"E4.10.0.1");var subQ10=sQuery(id+"F1.wireOp",EDGE,"E4.10.0.0");var subQ11=sQuery(id+"F1.wireOp",EDGE,"E4.9.0.1");var subQ12=sQuery(id+"F1.wireOp",EDGE,"E4.9.0.0");var subQ13=sQuery(id+"F1.wireOp",EDGE,"E4.8.0.1");var subQ14=sQuery(id+"F1.wireOp",EDGE,"E4.8.0.0");var subQ15=sQuery(id+"F1.wireOp",EDGE,"E4.7.0.1");var subQ16=sQuery(id+"F1.wireOp",EDGE,"E4.7.0.0");var subQ17=sQuery(id+"F1.wireOp",EDGE,"E4.6.0.1");var subQ18=sQuery(id+"F1.wireOp",EDGE,"E4.6.0.0");var subQ19=sQuery(id+"F1.wireOp",EDGE,"E4.5.0.1");var subQ20=sQuery(id+"F1.wireOp",EDGE,"E4.5.0.0");var subQ21=sQuery(id+"F1.wireOp",EDGE,"E4.4.0.1");var subQ22=sQuery(id+"F1.wireOp",EDGE,"E4.4.0.0");var subQ23=sQuery(id+"F1.wireOp",EDGE,"E4.3.0.1");var subQ24=sQuery(id+"F1.wireOp",EDGE,"E4.3.0.0");var subQ25=sQuery(id+"F1.wireOp",EDGE,"E4.2.0.1");var subQ26=sQuery(id+"F1.wireOp",EDGE,"E4.2.0.0");var subQ27=sQuery(id+"F1.wireOp",EDGE,"E4.1.0.1");var subQ28=sQuery(id+"F1.wireOp",EDGE,"E4.1.0.0");var subQ29=sQuery(id+"F1.wireOp",EDGE,"E3");var subQ30=sQuery(id+"F1.wireOp",EDGE,"E2");var subQ31=sQuery(id+"F1.wireOp",EDGE,"E0.left");var subQ32=sQuery(id+"F1.wireOp",EDGE,"E0.bottom");Q1=makeQuery(id+"FXmY1YLn0CrPCvh_1.boolean.opBoolean","MERGE",FACE,{"derivedFrom":[makeQuery(id+"F2.opExtrude","CAP_FACE",FACE,{"disambiguationData":[OSD([subQ32,subQ31,subQ30,subQ29,subQ28,subQ27,subQ26,subQ25,subQ24,subQ23,subQ22,subQ21,subQ20,subQ19,subQ18,subQ17,subQ16,subQ15,subQ14,subQ13,subQ12,subQ11,subQ10,subQ9,subQ8,subQ7,subQ6,subQ5,subQ4,subQ3,subQ2,subQ1,subQ0])],"isStart":false}),makeQuery(id+"FXmY1YLn0CrPCvh_1.opExtrude","CAP_FACE",FACE,{"disambiguationData":[OSD([subQ32,subQ31,subQ30,subQ29,subQ28,subQ27,subQ26,subQ25,subQ24,subQ23,subQ22,subQ21,subQ20,subQ19,subQ18,subQ17,subQ16,subQ15,subQ14,subQ13,subQ12,subQ11,subQ10,subQ9,subQ8,subQ7,subQ6,subQ5,subQ4,subQ3,subQ2,subQ1,subQ0])],"isStart":false})]});}
            extrude(context, id + "F10", {"entities" : qUnion([Q0]), "operationType" : NewBodyOperationType.REMOVE, "endBound" : BoundingType.THROUGH_ALL, "oppositeDirection" : true, "endBoundEntityFace" : qUnion([Q1]), "depth" : 25 * mm});
        }
    });
